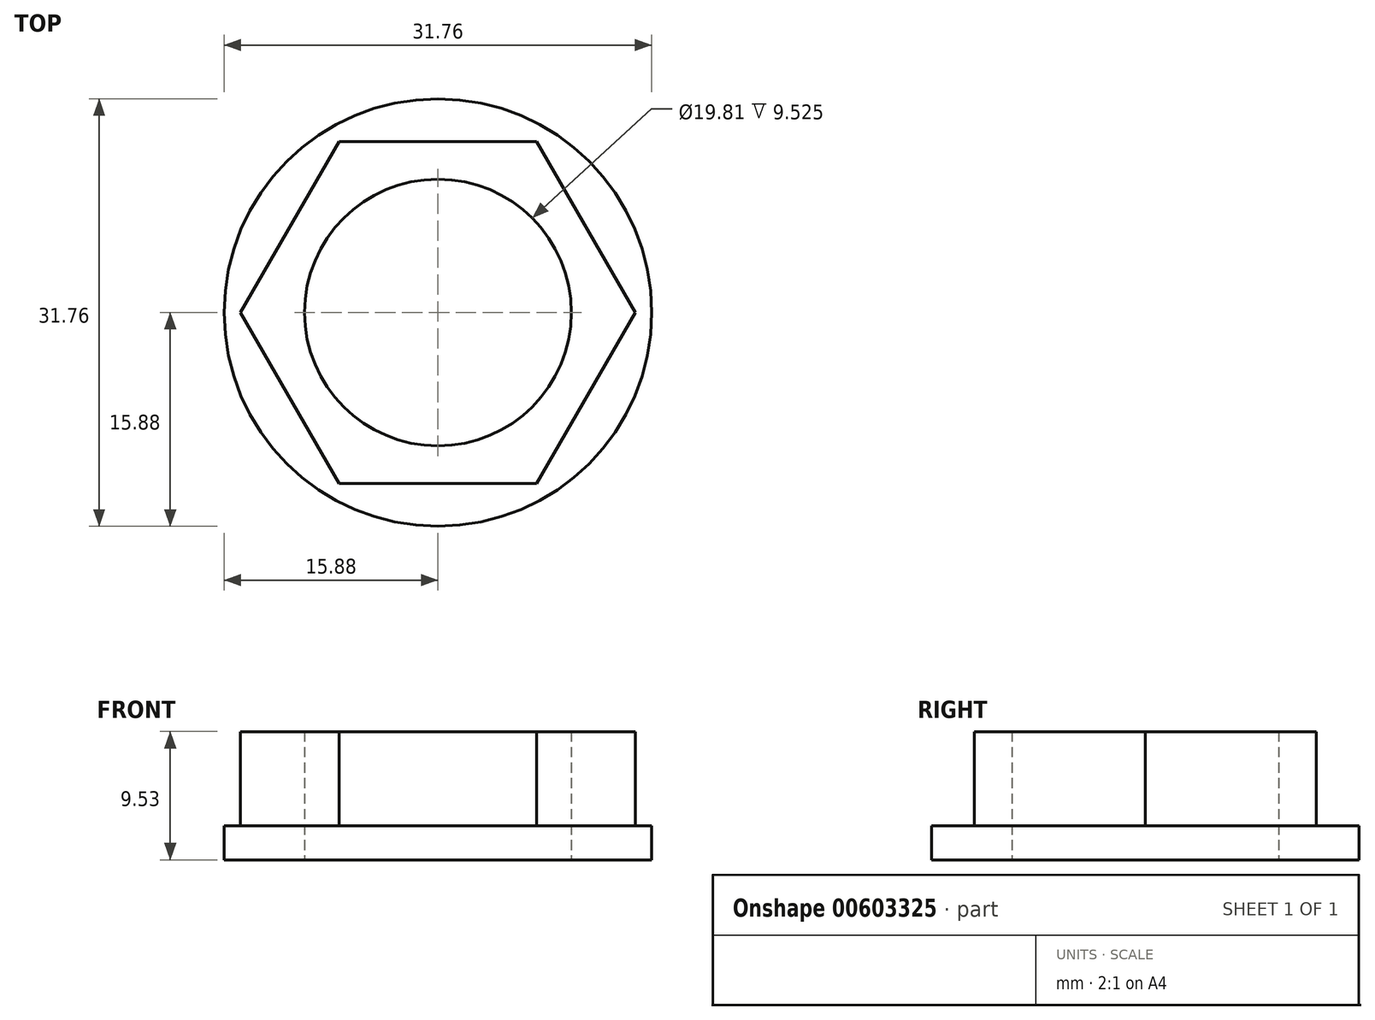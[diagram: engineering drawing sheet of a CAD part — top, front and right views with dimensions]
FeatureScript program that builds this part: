
annotation { "Feature Type Name" : "Feature", "Feature Type Description" : "" }
export const myFeature = defineFeature(function(context is Context, id is Id, definition is map)
    precondition{}
    {
        {
            var Q0;
            Q0=qCreatedBy(makeId("Top.planeOp"),FACE);
            var sketch = newSketch(context, id + "F0", { "sketchPlane" : qUnion([Q0])});
            skCircle(sketch, "E0", {"center": v(0, 0) * mm, "radius": 9.9 * mm});
            skCircle(sketch, "E1", {"center": v(0, 0) * mm, "radius": 14.66 * mm, "construction": true});
            skLineSegment(sketch, "E2", {"start": v(-7.33, 12.7) * mm, "end": v(7.33, 12.7) * mm});
            skLineSegment(sketch, "E3", {"start": v(-7.33, -12.7) * mm, "end": v(7.33, -12.7) * mm});
            skLineSegment(sketch, "E4", {"start": v(-7.33, 12.7) * mm, "end": v(-14.66, 0) * mm});
            skLineSegment(sketch, "E5", {"start": v(-14.66, 0) * mm, "end": v(-7.33, -12.7) * mm});
            skLineSegment(sketch, "E6", {"start": v(7.33, -12.7) * mm, "end": v(14.66, 0) * mm});
            skLineSegment(sketch, "E7", {"start": v(14.66, 0) * mm, "end": v(7.33, 12.7) * mm});
            skSolve(sketch);
        }
        {
            var Q0;
            Q0 = qSketchRegion(id + "F0", true);
            extrude(context, id + "F1", {"entities" : qUnion([Q0]), "depth" : 9.52 * mm, "offsetDistance" : 25.4 * mm});
        }
        {
            var Q0;
            Q0=qCreatedBy(makeId("Top.planeOp"),FACE);
            var sketch = newSketch(context, id + "F2", { "sketchPlane" : qUnion([Q0])});
            skCircle(sketch, "E8", {"center": v(0, 0) * mm, "radius": 15.87 * mm});
            skCircle(sketch, "E9.0", {"center": v(0, 0) * mm, "radius": 9.9 * mm});
            skSolve(sketch);
        }
        {
            var Q0;
            Q0 = qSketchRegion(id + "F2", true);
            extrude(context, id + "F3", {"entities" : qUnion([Q0]), "operationType" : NewBodyOperationType.ADD, "depth" : 2.54 * mm, "offsetDistance" : 25.4 * mm});
        }
    });
